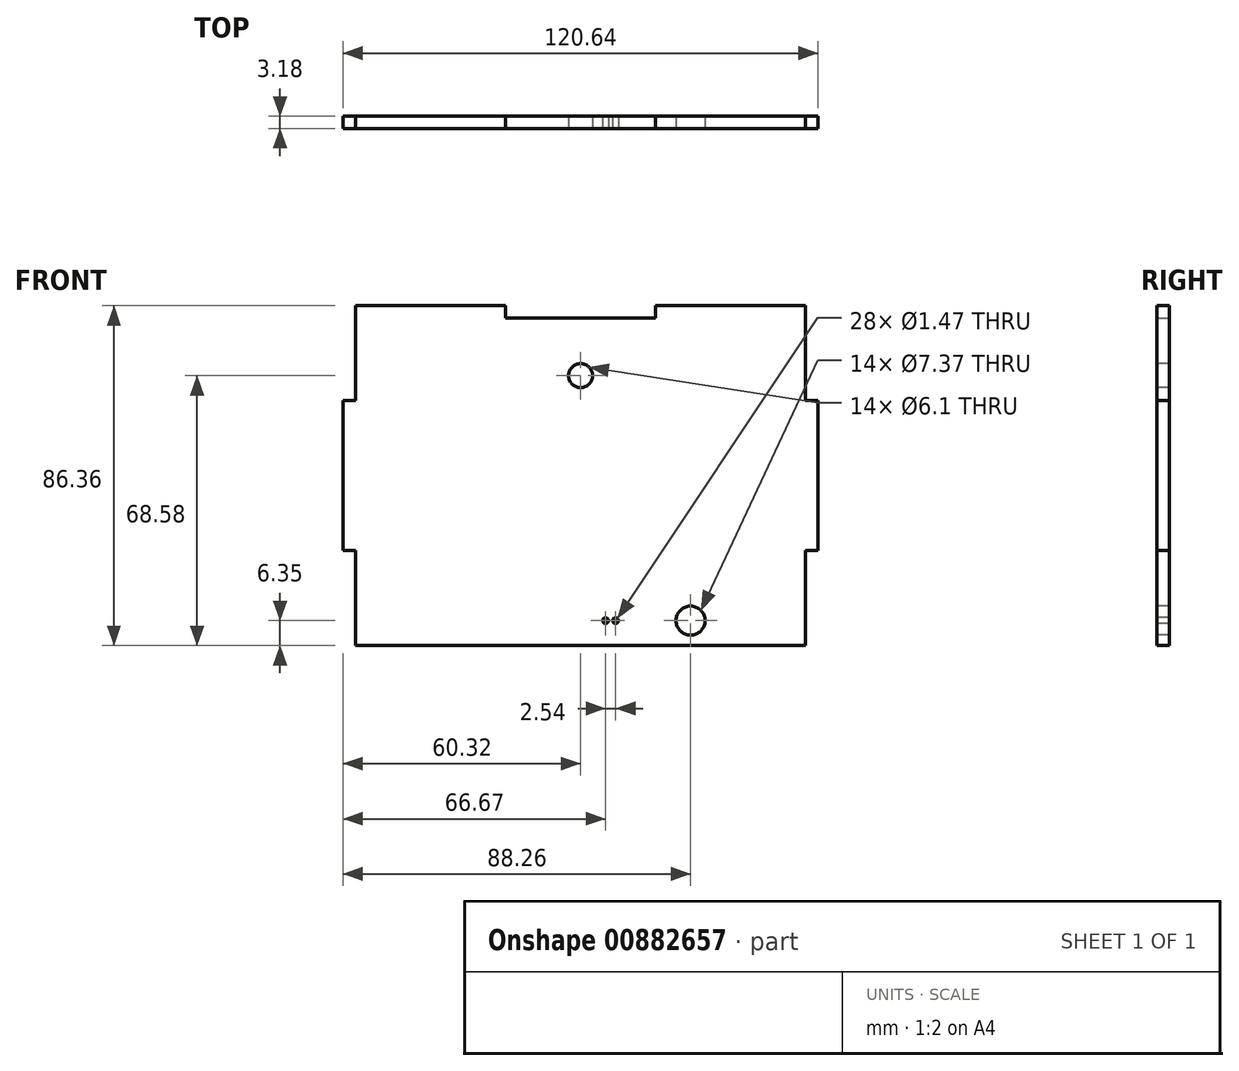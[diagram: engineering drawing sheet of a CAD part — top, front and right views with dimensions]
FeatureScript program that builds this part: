
annotation { "Feature Type Name" : "Feature", "Feature Type Description" : "" }
export const myFeature = defineFeature(function(context is Context, id is Id, definition is map)
    precondition{}
    {
        {
            var Q0;
            Q0=qCreatedBy(makeId("Front.planeOp"),FACE);
            var sketch = newSketch(context, id + "F0", { "sketchPlane" : qUnion([Q0])});
            skLineSegment(sketch, "E0.bottom", {"start": v(60.33, -43.18) * mm, "end": v(-60.33, -43.18) * mm});
            skLineSegment(sketch, "E0.top", {"start": v(60.33, 43.18) * mm, "end": v(-60.33, 43.18) * mm});
            skLineSegment(sketch, "E0.left", {"start": v(60.33, -43.18) * mm, "end": v(60.33, 43.18) * mm});
            skLineSegment(sketch, "E0.right", {"start": v(-60.33, -43.18) * mm, "end": v(-60.33, 43.18) * mm});
            skPoint(sketch, "E0.middle", {"position": v(0, 0) * mm});
            skLineSegment(sketch, "E1", {"start": v(0, 43.18) * mm, "end": v(19.05, 43.18) * mm});
            skLineSegment(sketch, "E2", {"start": v(0, 43.18) * mm, "end": v(-19.05, 43.18) * mm});
            skLineSegment(sketch, "E3", {"start": v(-19.05, 43.18) * mm, "end": v(-19.05, 40) * mm});
            skLineSegment(sketch, "E4", {"start": v(19.05, 43.18) * mm, "end": v(19.05, 40) * mm});
            skLineSegment(sketch, "E5", {"start": v(19.05, 40) * mm, "end": v(-19.05, 40) * mm});
            skLineSegment(sketch, "E6", {"start": v(-60.33, 0) * mm, "end": v(-60.33, 19.05) * mm});
            skLineSegment(sketch, "E7", {"start": v(-60.33, 0) * mm, "end": v(-60.33, -19.05) * mm});
            skLineSegment(sketch, "E8", {"start": v(-60.33, -19.05) * mm, "end": v(-57.15, -19.05) * mm});
            skLineSegment(sketch, "E9", {"start": v(-57.15, -19.05) * mm, "end": v(-57.15, -43.18) * mm});
            skLineSegment(sketch, "E10", {"start": v(-60.33, 19.05) * mm, "end": v(-57.15, 19.05) * mm});
            skLineSegment(sketch, "E11", {"start": v(-57.15, 19.05) * mm, "end": v(-57.15, 43.18) * mm});
            skLineSegment(sketch, "E12.MirrorCS", {"start": v(57.15, 19.05) * mm, "end": v(57.15, 43.18) * mm});
            skLineSegment(sketch, "E13.MirrorCS", {"start": v(57.15, -19.05) * mm, "end": v(57.15, -43.18) * mm});
            skLineSegment(sketch, "E14", {"start": v(57.15, 19.05) * mm, "end": v(60.33, 19.05) * mm});
            skLineSegment(sketch, "E15", {"start": v(57.15, -19.05) * mm, "end": v(60.33, -19.05) * mm});
            skSolve(sketch);
        }
        {
            var Q0;
            {var subQ2=sQuery(id+"F0.wireOp",EDGE,"E3");Q0=makeQuery(id+"F0.imprint","IMPRINT",FACE,{"disambiguationData":[TD([[makeQuery(id+"F0.imprint","IMPRINT",EDGE,{"derivedFrom":subQ2}),-1.0]])]});}
            var Q1;
            Q1=makeQuery(id+"F0.imprint","IMPRINT",FACE,{"disambiguationData":[TD([[makeQuery(id+"F0.imprint","IMPRINT",EDGE,{"derivedFrom":sQuery(id+"F0.wireOp",EDGE,"0iutSNji-cbNv-w4t3-Ue9f-pbIyJnXAomav")}),1.0]])]});
            var Q2;
            {var subQ4=sQuery(id+"F0.wireOp",EDGE,"E4");Q2=makeQuery(id+"F0.imprint","IMPRINT",FACE,{"disambiguationData":[TD([[makeQuery(id+"F0.imprint","IMPRINT",EDGE,{"derivedFrom":subQ4}),1.0]])]});}
            extrude(context, id + "F1", {"entities" : qUnion([Q0, Q1, Q2]), "depth" : 3.17 * mm, "offsetDistance" : 25.4 * mm});
        }
        {
            var Q0;
            Q0=makeQuery(id+"F1.opExtrude","CAP_FACE",FACE,{"disambiguationData":[OSD([sQuery(id+"F0.wireOp",EDGE,"E0.bottom"),sQuery(id+"F0.wireOp",EDGE,"E0.top"),sQuery(id+"F0.wireOp",EDGE,"E0.left"),sQuery(id+"F0.wireOp",EDGE,"E3"),sQuery(id+"F0.wireOp",EDGE,"E4"),sQuery(id+"F0.wireOp",EDGE,"E5"),sQuery(id+"F0.wireOp",EDGE,"E6"),sQuery(id+"F0.wireOp",EDGE,"E7"),sQuery(id+"F0.wireOp",EDGE,"E8"),sQuery(id+"F0.wireOp",EDGE,"E9"),sQuery(id+"F0.wireOp",EDGE,"E10"),sQuery(id+"F0.wireOp",EDGE,"E11"),sQuery(id+"F0.wireOp",EDGE,"E12.MirrorCS"),sQuery(id+"F0.wireOp",EDGE,"E13.MirrorCS"),sQuery(id+"F0.wireOp",EDGE,"E14"),sQuery(id+"F0.wireOp",EDGE,"E15")])],"isStart":false});
            var sketch = newSketch(context, id + "F2", { "sketchPlane" : qUnion([Q0])});
            skCircle(sketch, "E16", {"center": v(6.35, -36.83) * mm, "radius": 0.74 * mm});
            skCircle(sketch, "E17", {"center": v(8.9, -36.83) * mm, "radius": 0.74 * mm});
            skCircle(sketch, "E18", {"center": v(27.94, -36.83) * mm, "radius": 3.68 * mm});
            skCircle(sketch, "E19", {"center": v(0, 25.4) * mm, "radius": 3.05 * mm});
            skSolve(sketch);
        }
        {
            var Q0;
            Q0=makeQuery(id+"F2.imprint","IMPRINT",FACE,{"disambiguationData":[TD([[makeQuery(id+"F2.imprint","IMPRINT",EDGE,{"derivedFrom":sQuery(id+"F2.wireOp",EDGE,"E19")}),1.0]])]});
            var Q1;
            Q1=makeQuery(id+"F2.imprint","IMPRINT",FACE,{"disambiguationData":[TD([[makeQuery(id+"F2.imprint","IMPRINT",EDGE,{"derivedFrom":sQuery(id+"F2.wireOp",EDGE,"E18")}),1.0]])]});
            var Q2;
            Q2=makeQuery(id+"F2.imprint","IMPRINT",FACE,{"disambiguationData":[TD([[makeQuery(id+"F2.imprint","IMPRINT",EDGE,{"derivedFrom":sQuery(id+"F2.wireOp",EDGE,"E16")}),1.0]])]});
            var Q3;
            Q3=makeQuery(id+"F2.imprint","IMPRINT",FACE,{"disambiguationData":[TD([[makeQuery(id+"F2.imprint","IMPRINT",EDGE,{"derivedFrom":sQuery(id+"F2.wireOp",EDGE,"E17")}),1.0]])]});
            extrude(context, id + "F3", {"entities" : qUnion([Q0, Q1, Q2, Q3]), "operationType" : NewBodyOperationType.REMOVE, "endBound" : BoundingType.THROUGH_ALL, "oppositeDirection" : true, "depth" : 25.4 * mm, "offsetDistance" : 25.4 * mm});
        }
    });
